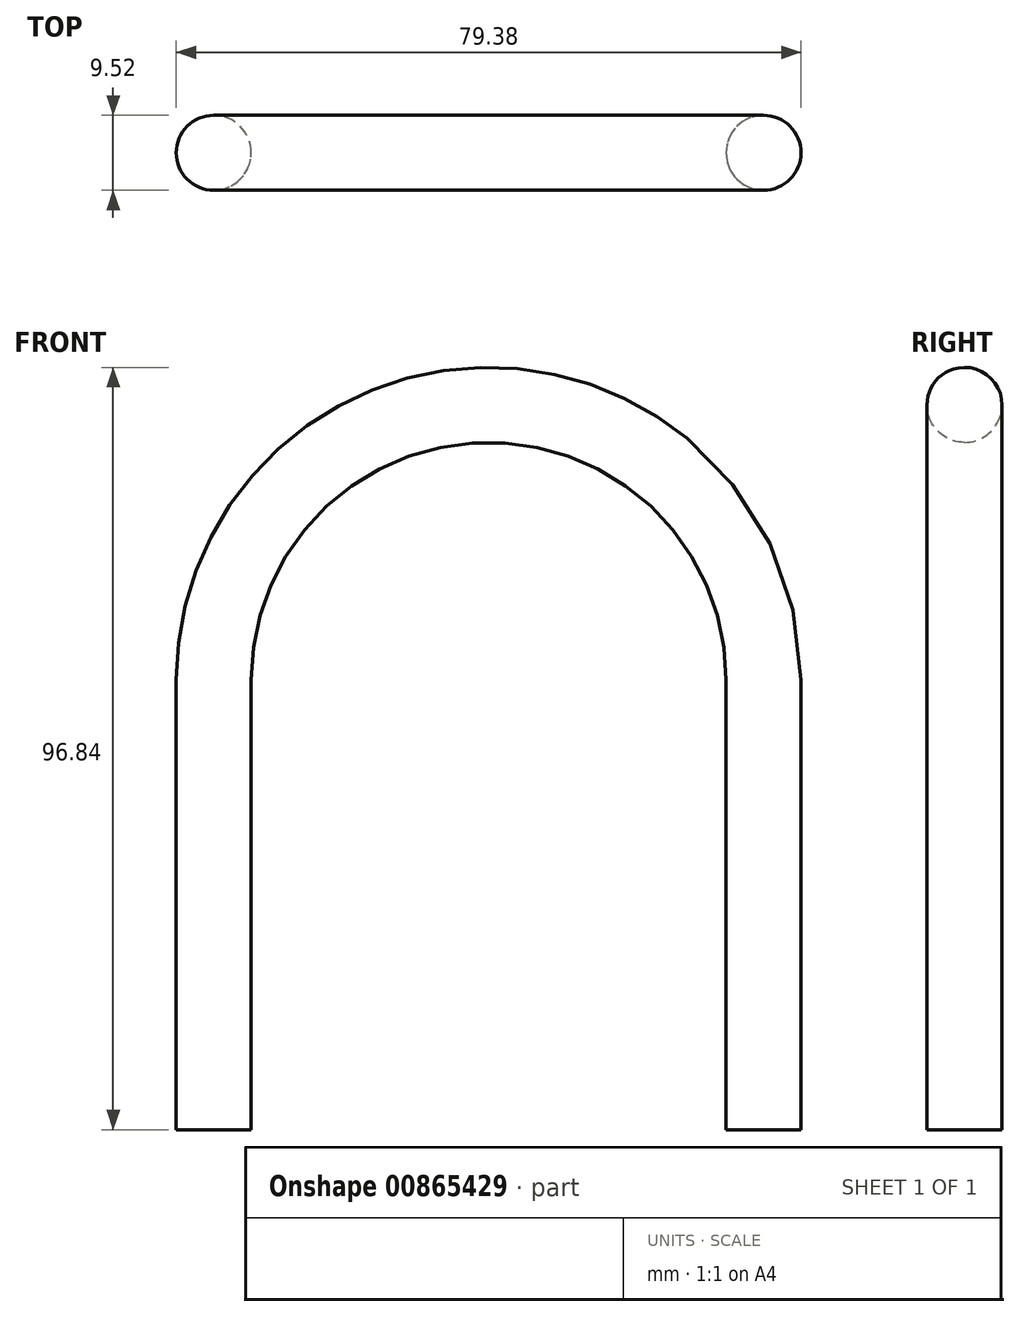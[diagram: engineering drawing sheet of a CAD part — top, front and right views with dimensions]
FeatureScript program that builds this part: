
annotation { "Feature Type Name" : "Feature", "Feature Type Description" : "" }
export const myFeature = defineFeature(function(context is Context, id is Id, definition is map)
    precondition{}
    {
        {
            var Q0;
            Q0=qCreatedBy(makeId("Front.planeOp"),FACE);
            var sketch = newSketch(context, id + "F0", { "sketchPlane" : qUnion([Q0])});
            skLineSegment(sketch, "E0", {"start": v(-34.93, 0) * mm, "end": v(-34.93, 57.15) * mm});
            skArc(sketch, "E1", {"start": v(0, 92.08) * mm, "mid": v(-24.7, 81.85) * mm, "end": v(-34.93, 57.15) * mm});
            skArc(sketch, "E2.MirrorCS", {"start": v(0, 92.08) * mm, "mid": v(24.7, 81.85) * mm, "end": v(34.92, 57.15) * mm});
            skLineSegment(sketch, "E3.MirrorCS", {"start": v(34.93, 0) * mm, "end": v(34.93, 57.15) * mm});
            skSolve(sketch);
        }
        {
            var Q0;
            Q0=qCreatedBy(makeId("Top.planeOp"),FACE);
            var sketch = newSketch(context, id + "F1", { "sketchPlane" : qUnion([Q0])});
            skCircle(sketch, "E4", {"center": v(-34.93, 0) * mm, "radius": 4.76 * mm});
            skSolve(sketch);
        }
        {
            var Q0;
            Q0=makeQuery(id+"F1.imprint","IMPRINT",FACE,{"disambiguationData":[TD([[makeQuery(id+"F1.imprint","IMPRINT",EDGE,{"derivedFrom":sQuery(id+"F1.wireOp",EDGE,"E4")}),1.0]])]});
            var Q1;
            Q1 = qConstructionFilter(qBodyType(qCreatedBy(id + "F0" ,EDGE), BodyType.WIRE), ConstructionObject.NO);
            sweep(context, id + "F2", {"profiles" : qUnion([Q0]), "path" : qUnion([Q1])});
        }
    });
